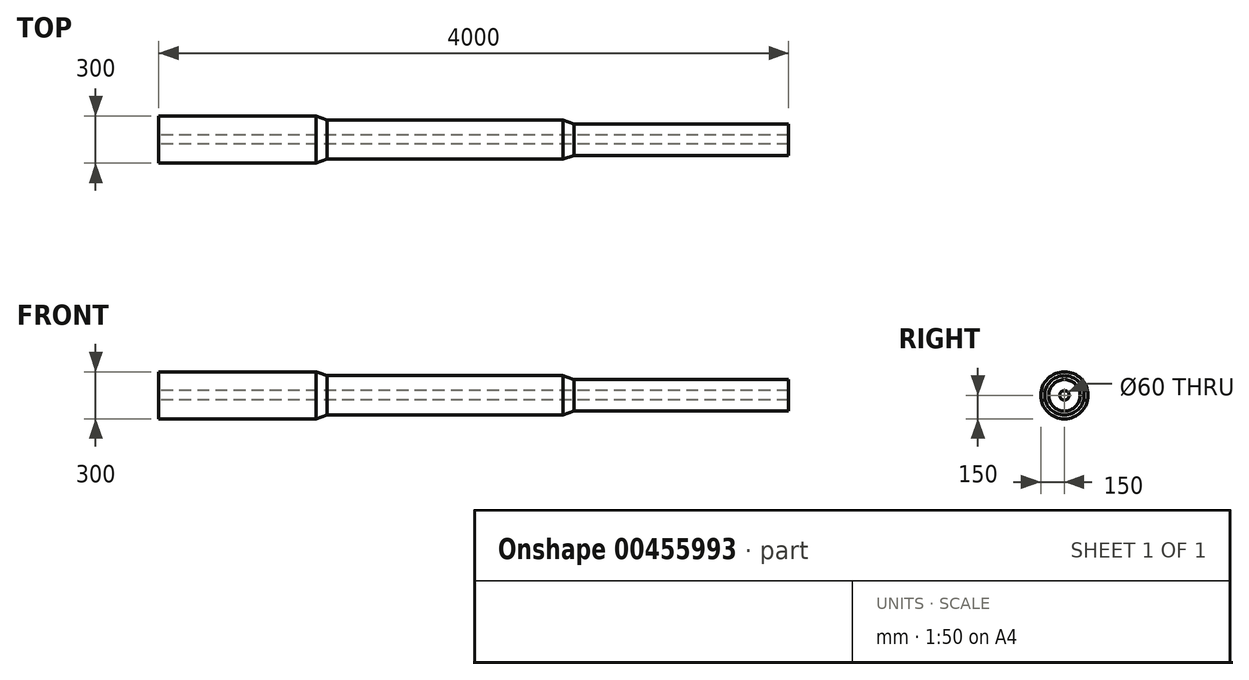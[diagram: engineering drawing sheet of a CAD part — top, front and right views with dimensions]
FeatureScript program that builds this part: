
annotation { "Feature Type Name" : "Feature", "Feature Type Description" : "" }
export const myFeature = defineFeature(function(context is Context, id is Id, definition is map)
    precondition{}
    {
        {
            var Q0;
            Q0=qCreatedBy(makeId("Front.planeOp"),FACE);
            var sketch = newSketch(context, id + "F0", { "sketchPlane" : qUnion([Q0])});
            skLineSegment(sketch, "E0", {"start": v(0, 0) * mm, "end": v(633, 0) * mm});
            skLineSegment(sketch, "E1", {"start": v(0, 30) * mm, "end": v(4000, 30) * mm});
            skLineSegment(sketch, "E2", {"start": v(4000, 30) * mm, "end": v(4000, 100) * mm});
            skLineSegment(sketch, "E3", {"start": v(4000, 100) * mm, "end": v(2637.37, 100) * mm});
            skLineSegment(sketch, "E4", {"start": v(2637.37, 100) * mm, "end": v(2568.69, 125) * mm});
            skLineSegment(sketch, "E5", {"start": v(2568.69, 125) * mm, "end": v(1068.69, 125) * mm});
            skLineSegment(sketch, "E6", {"start": v(1068.69, 125) * mm, "end": v(1000, 150) * mm});
            skLineSegment(sketch, "E7", {"start": v(1000, 150) * mm, "end": v(0, 150) * mm});
            skLineSegment(sketch, "E8", {"start": v(0, 150) * mm, "end": v(0, 30) * mm});
            skSolve(sketch);
        }
        {
            var Q0;
            Q0=makeQuery(id+"F0.imprint","IMPRINT",FACE,{"disambiguationData":[TD([[makeQuery(id+"F0.imprint","IMPRINT",EDGE,{"derivedFrom":sQuery(id+"F0.wireOp",EDGE,"E1")}),1.0]])]});
            var Q1;
            Q1=sQuery(id+"F0.wireOp",EDGE,"E0");
            revolve(context, id + "F1", {"entities" : qUnion([Q0]), "axis" : qUnion([Q1]), "revolveType" : RevolveType.FULL});
        }
    });
